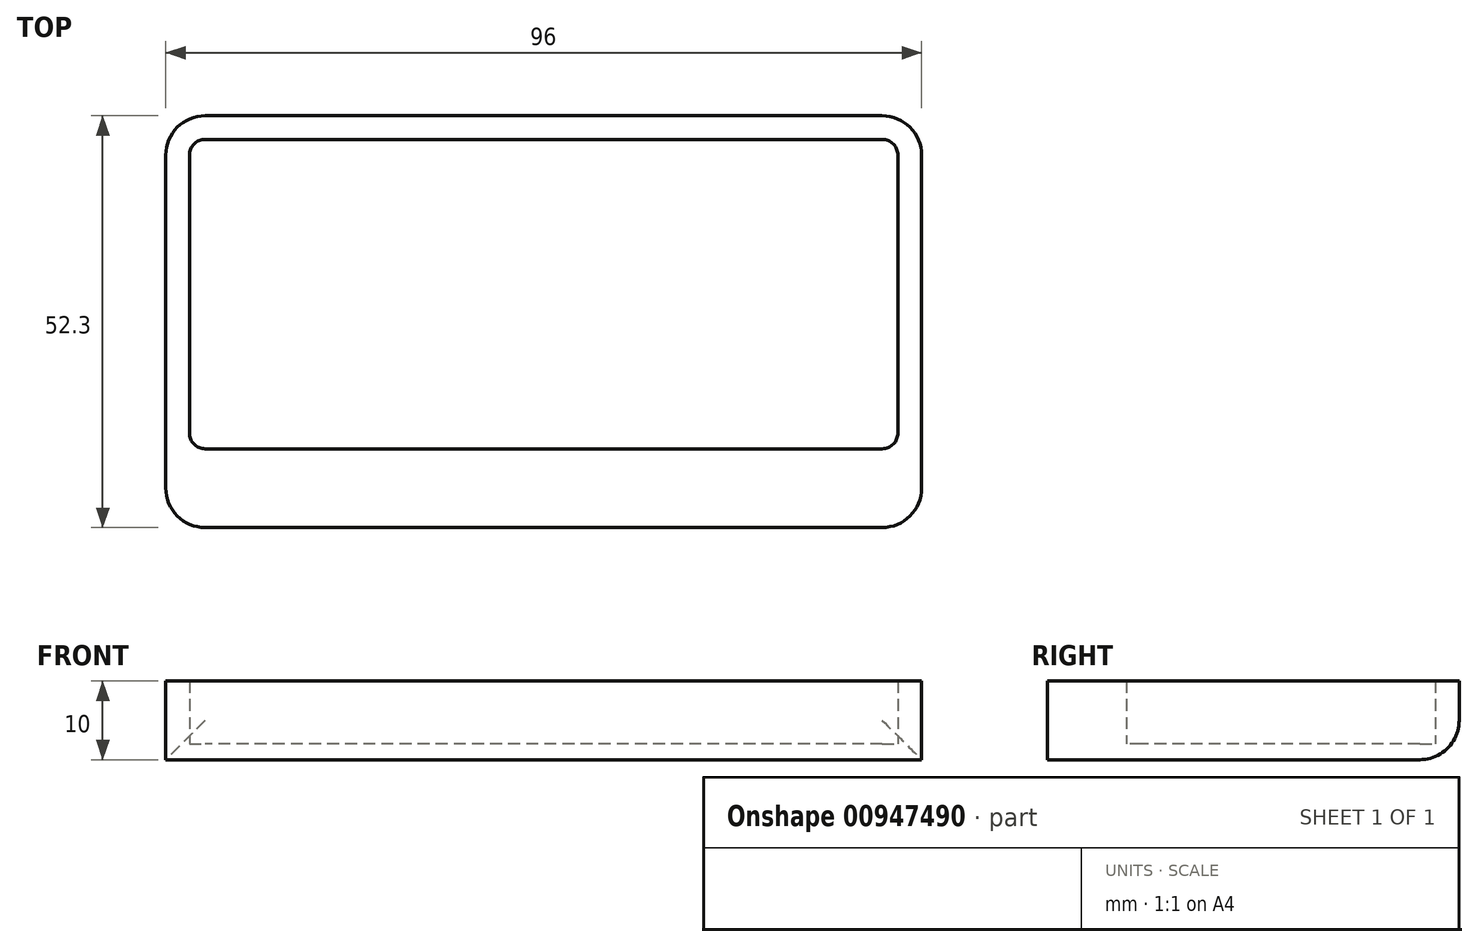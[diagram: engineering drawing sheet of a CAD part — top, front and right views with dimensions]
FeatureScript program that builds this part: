
annotation { "Feature Type Name" : "Feature", "Feature Type Description" : "" }
export const myFeature = defineFeature(function(context is Context, id is Id, definition is map)
    precondition{}
    {
        {
            var Q0;
            Q0=qCreatedBy(makeId("Top.planeOp"),FACE);
            var sketch = newSketch(context, id + "F0", { "sketchPlane" : qUnion([Q0])});
            skLineSegment(sketch, "E0.bottom", {"start": v(45, 19.65) * mm, "end": v(-45, 19.65) * mm});
            skLineSegment(sketch, "E0.top", {"start": v(45, -19.65) * mm, "end": v(-45, -19.65) * mm});
            skLineSegment(sketch, "E0.left", {"start": v(45, 19.65) * mm, "end": v(45, -19.65) * mm});
            skLineSegment(sketch, "E0.right", {"start": v(-45, 19.65) * mm, "end": v(-45, -19.65) * mm});
            skPoint(sketch, "E0.middle", {"position": v(0, 0) * mm});
            skLineSegment(sketch, "E1", {"start": v(45, -29.65) * mm, "end": v(-45, -29.65) * mm});
            skLineSegment(sketch, "E2", {"start": v(-45, -29.65) * mm, "end": v(-48, -29.65) * mm});
            skLineSegment(sketch, "E3", {"start": v(-48, -29.65) * mm, "end": v(-48, 19.65) * mm});
            skLineSegment(sketch, "E4", {"start": v(-48, 19.65) * mm, "end": v(-48, 22.65) * mm});
            skLineSegment(sketch, "E5.MirrorCS", {"start": v(48, -29.65) * mm, "end": v(48, 19.65) * mm});
            skLineSegment(sketch, "E6.MirrorCS", {"start": v(48, 19.65) * mm, "end": v(48, 22.65) * mm});
            skLineSegment(sketch, "E7.MirrorCS", {"start": v(45, -29.65) * mm, "end": v(48, -29.65) * mm});
            skLineSegment(sketch, "E8", {"start": v(-48, 22.65) * mm, "end": v(48, 22.65) * mm});
            skSolve(sketch);
        }
        {
            var Q0;
            Q0=makeQuery(id+"F0.imprint","IMPRINT",FACE,{"disambiguationData":[TD([[makeQuery(id+"F0.imprint","IMPRINT",EDGE,{"derivedFrom":sQuery(id+"F0.wireOp",EDGE,"E0.bottom")}),-1.0]])]});
            extrude(context, id + "F1", {"entities" : qUnion([Q0]), "depth" : 10 * mm, "offsetDistance" : 25 * mm});
        }
        {
            var Q0;
            Q0=makeQuery(id+"F0.imprint","IMPRINT",FACE,{"disambiguationData":[TD([[makeQuery(id+"F0.imprint","IMPRINT",EDGE,{"derivedFrom":sQuery(id+"F0.wireOp",EDGE,"E0.bottom")}),1.0]])]});
            extrude(context, id + "F2", {"entities" : qUnion([Q0]), "operationType" : NewBodyOperationType.ADD, "depth" : 2 * mm, "offsetDistance" : 25 * mm});
        }
        {
            var Q0;
            Q0=makeQuery(id+"F1.opExtrude","CAP_EDGE",EDGE,{"disambiguationData":[OSD([sQuery(id+"F0.wireOp",EDGE,"E8")])],"isStart":true});
            var Q1;
            Q1=makeQuery(id+"F1.opExtrude","SWEPT_EDGE",EDGE,{"disambiguationData":[OSD([sQuery(id+"F0.wireOp",EDGE,"E4"),sQuery(id+"F0.wireOp",EDGE,"E8")])]});
            var Q2;
            Q2=makeQuery(id+"F1.opExtrude","SWEPT_EDGE",EDGE,{"disambiguationData":[OSD([sQuery(id+"F0.wireOp",EDGE,"E6.MirrorCS"),sQuery(id+"F0.wireOp",EDGE,"E8")])]});
            var Q3;
            Q3=makeQuery(id+"F1.opExtrude","SWEPT_EDGE",EDGE,{"disambiguationData":[OSD([sQuery(id+"F0.wireOp",EDGE,"E2"),sQuery(id+"F0.wireOp",EDGE,"E3")])]});
            var Q4;
            Q4=makeQuery(id+"F1.opExtrude","SWEPT_EDGE",EDGE,{"disambiguationData":[OSD([sQuery(id+"F0.wireOp",EDGE,"E5.MirrorCS"),sQuery(id+"F0.wireOp",EDGE,"E7.MirrorCS")])]});
            fillet(context, id + "F3", {"entities" : qUnion([Q0, Q1, Q2, Q3, Q4]), "radius" : 5 * mm, "tangentPropagation" : true, "allowEdgeOverflow" : false});
        }
        {
            var Q0;
            Q0=makeQuery(id+"F1.opExtrude","SWEPT_EDGE",EDGE,{"disambiguationData":[OSD([sQuery(id+"F0.wireOp",EDGE,"E0.bottom"),sQuery(id+"F0.wireOp",EDGE,"E0.right")])]});
            var Q1;
            Q1=makeQuery(id+"F1.opExtrude","SWEPT_EDGE",EDGE,{"disambiguationData":[OSD([sQuery(id+"F0.wireOp",EDGE,"E0.bottom"),sQuery(id+"F0.wireOp",EDGE,"E0.left")])]});
            var Q2;
            Q2=makeQuery(id+"F1.opExtrude","SWEPT_EDGE",EDGE,{"disambiguationData":[OSD([sQuery(id+"F0.wireOp",EDGE,"E0.top"),sQuery(id+"F0.wireOp",EDGE,"E0.left")])]});
            var Q3;
            Q3=makeQuery(id+"F1.opExtrude","SWEPT_EDGE",EDGE,{"disambiguationData":[OSD([sQuery(id+"F0.wireOp",EDGE,"E0.top"),sQuery(id+"F0.wireOp",EDGE,"E0.right")])]});
            fillet(context, id + "F4", {"entities" : qUnion([Q0, Q1, Q2, Q3]), "radius" : 2 * mm, "tangentPropagation" : true, "allowEdgeOverflow" : false});
        }
    });
